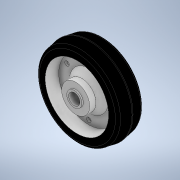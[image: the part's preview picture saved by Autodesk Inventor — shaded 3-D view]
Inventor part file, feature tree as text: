
AUTODESK INVENTOR PART (.ipt)
format: ipt  version: 2020 (Build 240168000, 168)  size: 232,448 bytes
history: native  units: mm
features: sketch x7, extrude x6, other x1, fillet x1, hole x1
ambient origin geometry x8: Origin, YZ Plane, XZ Plane, XY Plane, X Axis, Y Axis, Z Axis, Center Point
bodies: Body1 (feature_tree)
feature tree (16):
  other  "솔리드1"
  extrude  "돌출1"  Depth=20.0mm
  extrude  "돌출2"  Depth=27.0mm
  extrude  "돌출3"  Depth=56.0mm TaperAngle=0.0deg
  extrude  "돌출4"  Depth=50.0mm
  extrude  "돌출5"  Depth=51.0mm TaperAngle=0.0deg
  fillet  "모깎기1"  Radius=72.0mm
  hole  "구멍1"  [1 undecoded]
  extrude  "돌출6"  Depth=105.0mm
  sketch  "스케치1"
  sketch  "스케치2"
  sketch  "스케치3"
  sketch  "스케치4"
  sketch  "스케치5"
  sketch  "스케치6"
  sketch  "스케치7"
note: 1 required parameter value undecoded (feature->parameter linkage not recoverable at this tier; creation-order binding heuristic only, values carry confidence <= 0.55)
